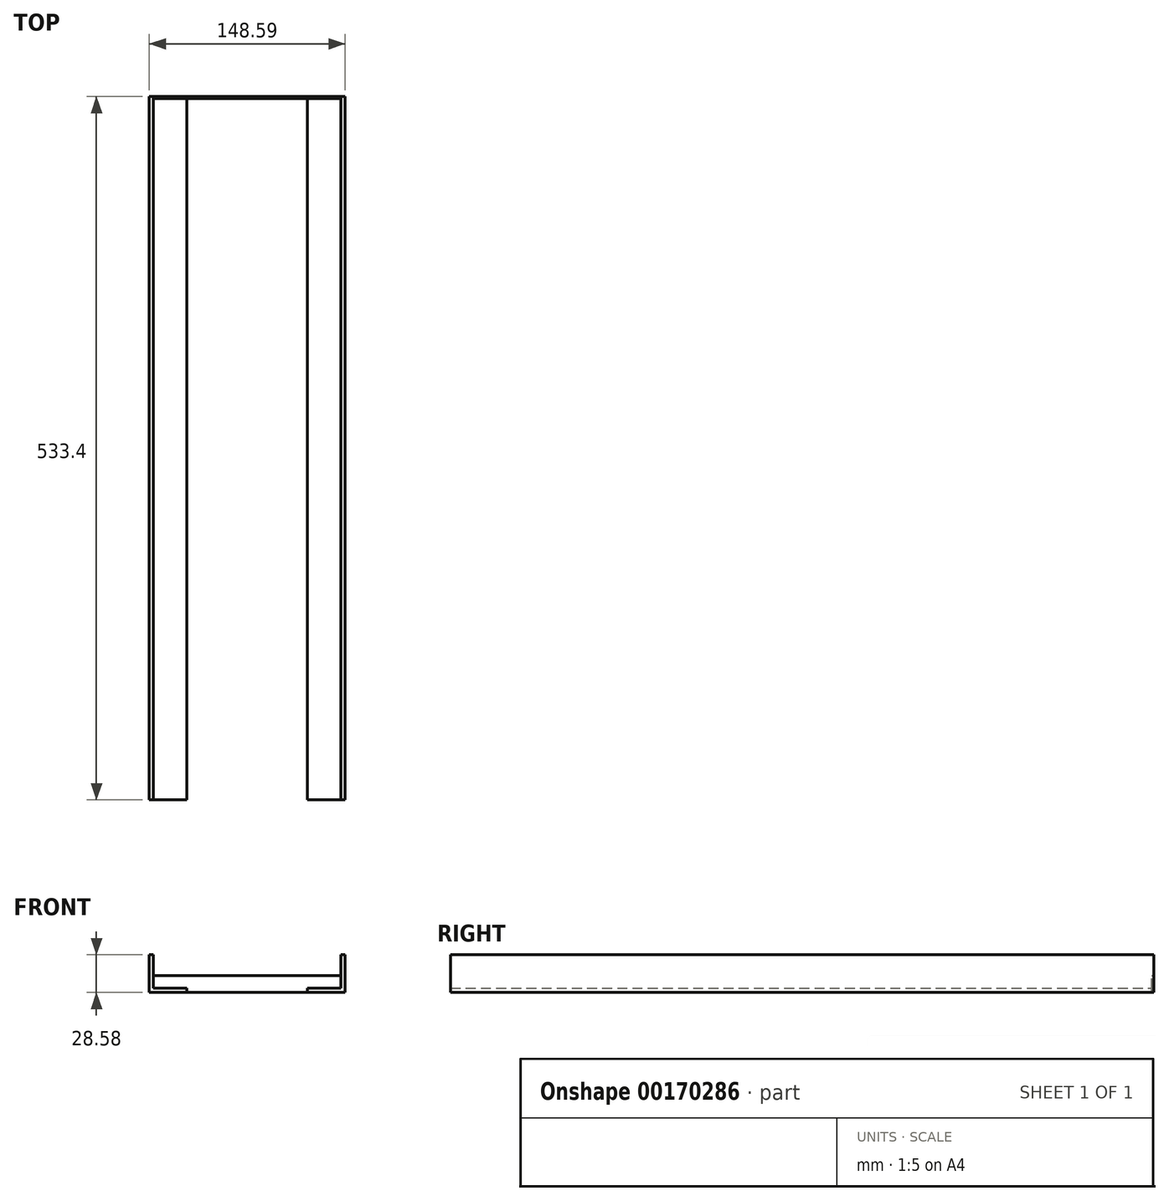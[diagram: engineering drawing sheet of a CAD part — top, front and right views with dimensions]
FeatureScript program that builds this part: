
annotation { "Feature Type Name" : "Feature", "Feature Type Description" : "" }
export const myFeature = defineFeature(function(context is Context, id is Id, definition is map)
    precondition{}
    {
        {
            var Q0;
            Q0=qCreatedBy(makeId("Front.planeOp"),FACE);
            var sketch = newSketch(context, id + "F0", { "sketchPlane" : qUnion([Q0])});
            skLineSegment(sketch, "E0", {"start": v(0, 0) * mm, "end": v(0, 25.4) * mm});
            skLineSegment(sketch, "E1", {"start": v(0, 25.4) * mm, "end": v(3.17, 25.4) * mm});
            skLineSegment(sketch, "E2", {"start": v(3.17, 25.4) * mm, "end": v(3.18, -3.18) * mm});
            skLineSegment(sketch, "E3", {"start": v(3.18, -3.18) * mm, "end": v(-25.4, -3.18) * mm});
            skLineSegment(sketch, "E4", {"start": v(-25.4, -3.18) * mm, "end": v(-25.4, 0) * mm});
            skLineSegment(sketch, "E5", {"start": v(-25.4, 0) * mm, "end": v(0, 0) * mm});
            skLineSegment(sketch, "E6.top", {"start": v(0, 9.52) * mm, "end": v(-25.4, 9.52) * mm});
            skLineSegment(sketch, "E6.left", {"start": v(3.18, -3.18) * mm, "end": v(3.18, 9.52) * mm});
            skLineSegment(sketch, "E6.right", {"start": v(-25.4, 0) * mm, "end": v(-25.4, 9.52) * mm});
            skLineSegment(sketch, "E7", {"start": v(-25.4, -3.18) * mm, "end": v(-116.84, -3.18) * mm});
            skLineSegment(sketch, "E8", {"start": v(-116.84, -3.18) * mm, "end": v(-116.84, 0) * mm});
            skLineSegment(sketch, "E9", {"start": v(-116.84, 0) * mm, "end": v(-142.24, 0) * mm});
            skLineSegment(sketch, "E10", {"start": v(-142.24, 0) * mm, "end": v(-142.24, 25.4) * mm});
            skLineSegment(sketch, "E11", {"start": v(-142.24, 25.4) * mm, "end": v(-145.42, 25.4) * mm});
            skLineSegment(sketch, "E12", {"start": v(-145.42, 25.4) * mm, "end": v(-145.42, -3.17) * mm});
            skLineSegment(sketch, "E13", {"start": v(-145.42, -3.17) * mm, "end": v(-116.84, -3.18) * mm});
            skLineSegment(sketch, "E14.bottom", {"start": v(-145.42, -3.18) * mm, "end": v(-116.84, -3.18) * mm});
            skLineSegment(sketch, "E14.top", {"start": v(-142.24, 9.53) * mm, "end": v(-116.84, 9.53) * mm});
            skLineSegment(sketch, "E14.left", {"start": v(-145.42, -3.17) * mm, "end": v(-145.42, 9.53) * mm});
            skLineSegment(sketch, "E14.right", {"start": v(-116.84, -3.17) * mm, "end": v(-116.84, 9.53) * mm});
            skLineSegment(sketch, "E15", {"start": v(-116.84, 0) * mm, "end": v(-25.4, 0) * mm});
            skLineSegment(sketch, "E16", {"start": v(-25.4, 9.52) * mm, "end": v(-116.84, 9.53) * mm});
            skSolve(sketch);
        }
        {
            var Q0;
            Q0=makeQuery(id+"F0.imprint","IMPRINT",FACE,{"disambiguationData":[TD([[makeQuery(id+"F0.imprint","IMPRINT",EDGE,{"derivedFrom":sQuery(id+"F0.wireOp",EDGE,"E1")}),-1.0]])]});
            var Q1;
            Q1=makeQuery(id+"F0.imprint","IMPRINT",FACE,{"disambiguationData":[TD([[makeQuery(id+"F0.imprint","IMPRINT",EDGE,{"derivedFrom":sQuery(id+"F0.wireOp",EDGE,"E8")}),1.0]])]});
            var Q2;
            {var subQ3=sQuery(id+"F0.wireOp",EDGE,"E9");Q2=makeQuery(id+"F0.imprint","IMPRINT",FACE,{"disambiguationData":[TD([[makeQuery(id+"F0.imprint","IMPRINT",EDGE,{"derivedFrom":subQ3}),1.0]])]});}
            extrude(context, id + "F1", {"entities" : qUnion([Q0, Q1, Q2]), "depth" : 533.4 * mm});
        }
        {
            var Q0;
            {var subQ0=sQuery(id+"F0.wireOp",EDGE,"E5");Q0=makeQuery(id+"F0.imprint","IMPRINT",FACE,{"disambiguationData":[TD([[makeQuery(id+"F0.imprint","IMPRINT",EDGE,{"derivedFrom":subQ0}),1.0]])]});}
            var Q1;
            {var subQ0=sQuery(id+"F0.wireOp",EDGE,"E9");Q1=makeQuery(id+"F0.imprint","IMPRINT",FACE,{"disambiguationData":[TD([[makeQuery(id+"F0.imprint","IMPRINT",EDGE,{"derivedFrom":subQ0}),-1.0]])]});}
            var Q2;
            Q2=makeQuery(id+"F0.imprint","IMPRINT",FACE,{"disambiguationData":[TD([[makeQuery(id+"F0.imprint","IMPRINT",EDGE,{"derivedFrom":sQuery(id+"F0.wireOp",EDGE,"E4")}),1.0]])]});
            var Q3;
            Q3=makeQuery(id+"F0.imprint","IMPRINT",FACE,{"disambiguationData":[TD([[makeQuery(id+"F0.imprint","IMPRINT",EDGE,{"derivedFrom":sQuery(id+"F0.wireOp",EDGE,"E6.right")}),1.0]])]});
            extrude(context, id + "F2", {"entities" : qUnion([Q0, Q1, Q2, Q3]), "operationType" : NewBodyOperationType.ADD, "depth" : 1.59 * mm});
        }
    });
